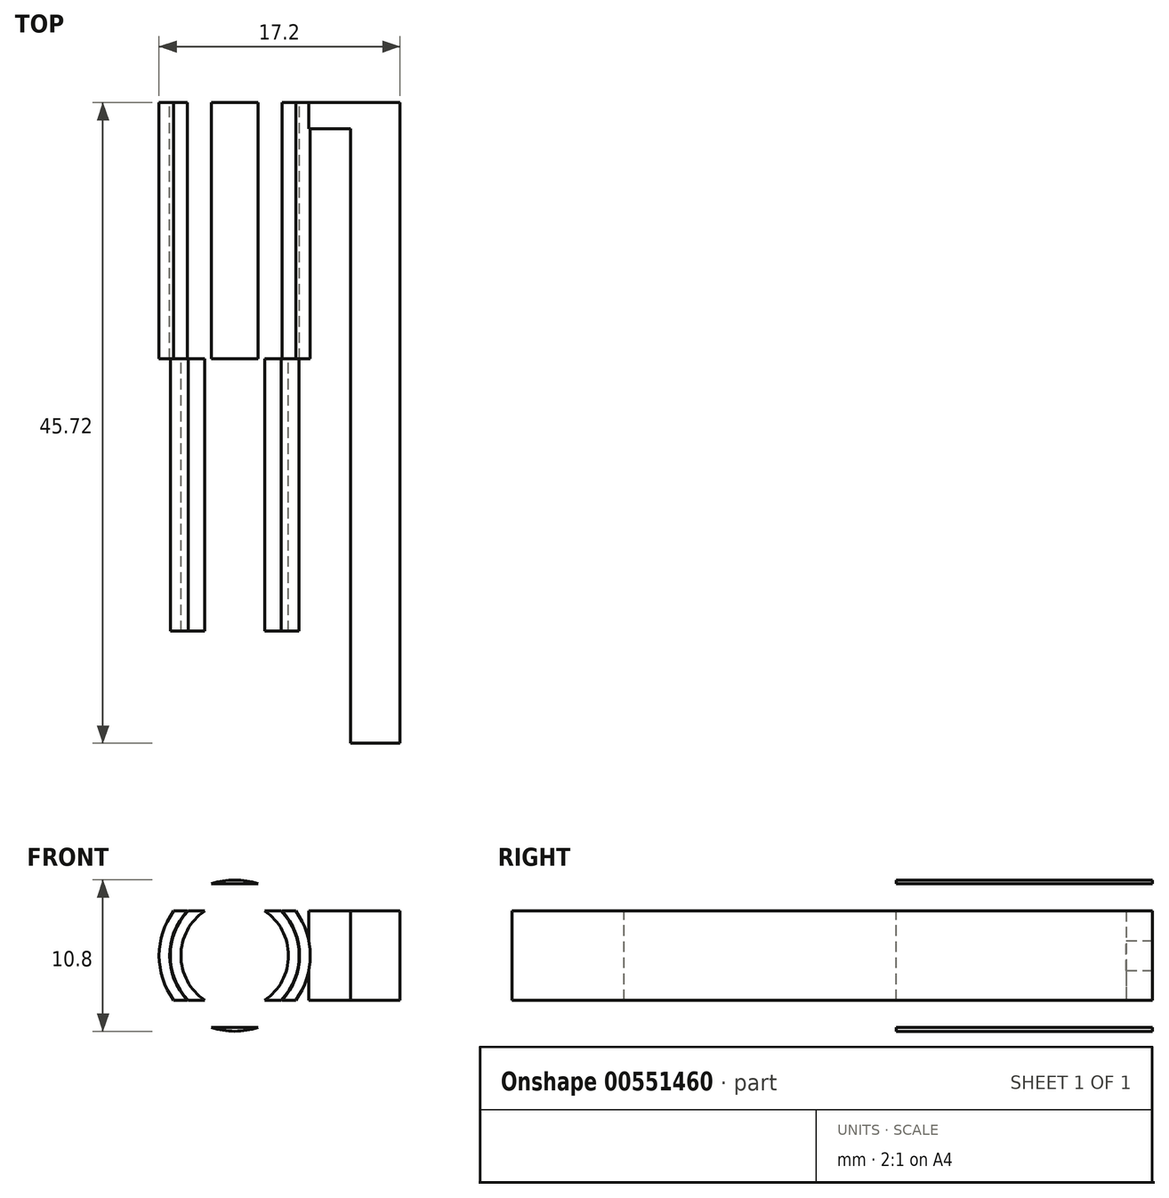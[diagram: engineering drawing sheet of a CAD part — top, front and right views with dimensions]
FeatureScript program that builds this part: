
annotation { "Feature Type Name" : "Feature", "Feature Type Description" : "" }
export const myFeature = defineFeature(function(context is Context, id is Id, definition is map)
    precondition{}
    {
        {
            var Q0;
            Q0=qCreatedBy(makeId("Front.planeOp"),FACE);
            var sketch = newSketch(context, id + "F0", { "sketchPlane" : qUnion([Q0])});
            skCircle(sketch, "E0", {"center": v(0, 0) * mm, "radius": 5.4 * mm});
            skSolve(sketch);
        }
        {
            var Q0;
            Q0=makeQuery(id+"F0.imprint","IMPRINT",FACE,{"disambiguationData":[TD([[makeQuery(id+"F0.imprint","IMPRINT",EDGE,{"derivedFrom":sQuery(id+"F0.wireOp",EDGE,"E0")}),1.0]])]});
            extrude(context, id + "F1", {"entities" : qUnion([Q0]), "depth" : 18.29 * mm, "offsetDistance" : 25.4 * mm});
        }
        {
            var Q0;
            Q0=makeQuery(id+"F1.opExtrude","CAP_FACE",FACE,{"disambiguationData":[OSD([sQuery(id+"F0.wireOp",EDGE,"E0")])],"isStart":true});
            var Q1;
            Q1=makeQuery(id+"F1.opExtrude","CAP_FACE",FACE,{"disambiguationData":[OSD([sQuery(id+"F0.wireOp",EDGE,"E0")])],"isStart":false});
            shell(context, id + "F2", {"entities" : qUnion([Q0, Q1]), "thickness" : 0.76 * mm});
        }
        {
            var Q0;
            Q0=makeQuery(id+"F1.opExtrude","CAP_FACE",FACE,{"disambiguationData":[OSD([sQuery(id+"F0.wireOp",EDGE,"E0")])],"isStart":false});
            var sketch = newSketch(context, id + "F3", { "sketchPlane" : qUnion([Q0])});
            skCircle(sketch, "E1", {"center": v(0, 0) * mm, "radius": 4.6 * mm});
            skSolve(sketch);
        }
        {
            var Q0;
            Q0=makeQuery(id+"F3.imprint","IMPRINT",FACE,{"disambiguationData":[TD([[makeQuery(id+"F3.imprint","IMPRINT",EDGE,{"derivedFrom":sQuery(id+"F3.wireOp",EDGE,"E1")}),1.0]])]});
            extrude(context, id + "F4", {"entities" : qUnion([Q0]), "depth" : 19.43 * mm, "offsetDistance" : 25.4 * mm});
        }
        {
            var Q0;
            Q0=makeQuery(id+"F4.opExtrude","CAP_FACE",FACE,{"disambiguationData":[OSD([sQuery(id+"F3.wireOp",EDGE,"E1")])],"isStart":false});
            var Q1;
            Q1=makeQuery(id+"F4.opExtrude","CAP_FACE",FACE,{"disambiguationData":[OSD([sQuery(id+"F3.wireOp",EDGE,"E1")])],"isStart":true});
            shell(context, id + "F5", {"entities" : qUnion([Q0, Q1]), "thickness" : 0.76 * mm});
        }
        {
            var Q0;
            Q0=makeQuery(id+"F1.opExtrude","CAP_FACE",FACE,{"disambiguationData":[OSD([sQuery(id+"F0.wireOp",EDGE,"E0")])],"isStart":true});
            var sketch = newSketch(context, id + "F6", { "sketchPlane" : qUnion([Q0])});
            skLineSegment(sketch, "E2", {"start": v(-7.1, 5.13) * mm, "end": v(-7.1, -5.13) * mm});
            skLineSegment(sketch, "E3", {"start": v(-7.1, -5.13) * mm, "end": v(-11.8, -5.13) * mm});
            skLineSegment(sketch, "E4", {"start": v(-11.8, -5.13) * mm, "end": v(-11.8, 5.13) * mm});
            skLineSegment(sketch, "E5", {"start": v(-11.8, 5.13) * mm, "end": v(-7.1, 5.13) * mm});
            skSolve(sketch);
        }
        {
            var Q0;
            Q0=makeQuery(id+"F6.imprint","IMPRINT",FACE,{"disambiguationData":[TD([[makeQuery(id+"F6.imprint","IMPRINT",EDGE,{"derivedFrom":sQuery(id+"F6.wireOp",EDGE,"E2")}),-1.0]])]});
            extrude(context, id + "F7", {"entities" : qUnion([Q0]), "oppositeDirection" : true, "depth" : 45.72 * mm, "offsetDistance" : 25.4 * mm});
        }
        {
            var Q0;
            Q0=makeQuery(id+"F7.opExtrude","SWEPT_FACE",FACE,{"disambiguationData":[OSD([sQuery(id+"F6.wireOp",EDGE,"E3")])]});
            var sketch = newSketch(context, id + "F8", { "sketchPlane" : qUnion([Q0])});
            skLineSegment(sketch, "E6", {"start": v(10.57, 45.72) * mm, "end": v(10.57, 0) * mm});
            skSolve(sketch);
        }
        {
            var Q0;
            {var subQ0=sQuery(id+"F8.wireOp",EDGE,"E6");Q0=makeQuery(id+"F8.imprint","IMPRINT",FACE,{"disambiguationData":[TD([[makeQuery(id+"F8.imprint","IMPRINT",EDGE,{"derivedFrom":subQ0}),-1.0]])]});}
            extrude(context, id + "F9", {"entities" : qUnion([Q0]), "operationType" : NewBodyOperationType.REMOVE, "oppositeDirection" : true, "depth" : 25.4 * mm, "offsetDistance" : 25.4 * mm});
        }
        {
            var Q0;
            Q0=makeQuery(id+"F7.opExtrude","SWEPT_FACE",FACE,{"disambiguationData":[OSD([sQuery(id+"F6.wireOp",EDGE,"E4")])]});
            var sketch = newSketch(context, id + "F10", { "sketchPlane" : qUnion([Q0])});
            skLineSegment(sketch, "E7", {"start": v(0, -3.18) * mm, "end": v(-45.72, -3.18) * mm});
            skLineSegment(sketch, "E8.MirrorCS", {"start": v(0, 3.18) * mm, "end": v(-45.72, 3.18) * mm});
            skSolve(sketch);
        }
        {
            var Q0;
            {var subQ0=sQuery(id+"F10.wireOp",EDGE,"E8.MirrorCS");Q0=makeQuery(id+"F10.imprint","IMPRINT",FACE,{"disambiguationData":[TD([[makeQuery(id+"F10.imprint","IMPRINT",EDGE,{"derivedFrom":subQ0}),-1.0]])]});}
            var Q1;
            {var subQ0=sQuery(id+"F10.wireOp",EDGE,"E7");Q1=makeQuery(id+"F10.imprint","IMPRINT",FACE,{"disambiguationData":[TD([[makeQuery(id+"F10.imprint","IMPRINT",EDGE,{"derivedFrom":subQ0}),1.0]])]});}
            extrude(context, id + "F11", {"entities" : qUnion([Q0, Q1]), "operationType" : NewBodyOperationType.REMOVE, "oppositeDirection" : true, "depth" : 25.4 * mm, "offsetDistance" : 25.4 * mm});
        }
        {
            var Q0;
            Q0=makeQuery(id+"F9.boolean.opBoolean","COPY",FACE,{"derivedFrom":makeQuery(id+"F9.opExtrude","SWEPT_FACE",FACE,{"disambiguationData":[OSD([sQuery(id+"F8.wireOp",EDGE,"E6")])]})});
            var sketch = newSketch(context, id + "F12", { "sketchPlane" : qUnion([Q0])});
            skLineSegment(sketch, "E9.bottom", {"start": v(0, 3.18) * mm, "end": v(1.87, 3.18) * mm});
            skLineSegment(sketch, "E9.top", {"start": v(0, -3.18) * mm, "end": v(1.87, -3.18) * mm});
            skLineSegment(sketch, "E9.left", {"start": v(0, 3.18) * mm, "end": v(0, -3.18) * mm});
            skLineSegment(sketch, "E9.right", {"start": v(1.87, 3.18) * mm, "end": v(1.87, -3.18) * mm});
            skSolve(sketch);
        }
        {
            var Q0;
            Q0=makeQuery(id+"F12.imprint","IMPRINT",FACE,{"disambiguationData":[TD([[makeQuery(id+"F12.imprint","IMPRINT",EDGE,{"derivedFrom":sQuery(id+"F12.wireOp",EDGE,"E9.bottom")}),1.0]])]});
            extrude(context, id + "F13", {"entities" : qUnion([Q0]), "operationType" : NewBodyOperationType.ADD, "depth" : 5.28 * mm, "offsetDistance" : 25.4 * mm});
        }
        {
            var Q0;
            Q0=makeQuery(id+"F9.boolean.opBoolean","COPY",FACE,{"derivedFrom":makeQuery(id+"F9.opExtrude","SWEPT_FACE",FACE,{"disambiguationData":[OSD([sQuery(id+"F8.wireOp",EDGE,"E6")])]})});
            var sketch = newSketch(context, id + "F14", { "sketchPlane" : qUnion([Q0])});
            skLineSegment(sketch, "E10.bottom", {"start": v(45.72, -3.18) * mm, "end": v(1.87, -3.18) * mm});
            skLineSegment(sketch, "E10.top", {"start": v(45.72, 3.18) * mm, "end": v(1.87, 3.18) * mm});
            skLineSegment(sketch, "E10.left", {"start": v(45.72, -3.18) * mm, "end": v(45.72, 3.18) * mm});
            skLineSegment(sketch, "E10.right", {"start": v(1.87, -3.18) * mm, "end": v(1.87, 3.18) * mm});
            skSolve(sketch);
        }
        {
            var Q0;
            Q0=makeQuery(id+"F14.imprint","IMPRINT",FACE,{"disambiguationData":[TD([[makeQuery(id+"F14.imprint","IMPRINT",EDGE,{"derivedFrom":sQuery(id+"F14.wireOp",EDGE,"E10.bottom")}),-1.0]])]});
            extrude(context, id + "F15", {"entities" : qUnion([Q0]), "operationType" : NewBodyOperationType.ADD, "depth" : 2.3 * mm, "offsetDistance" : 25.4 * mm});
        }
    });
